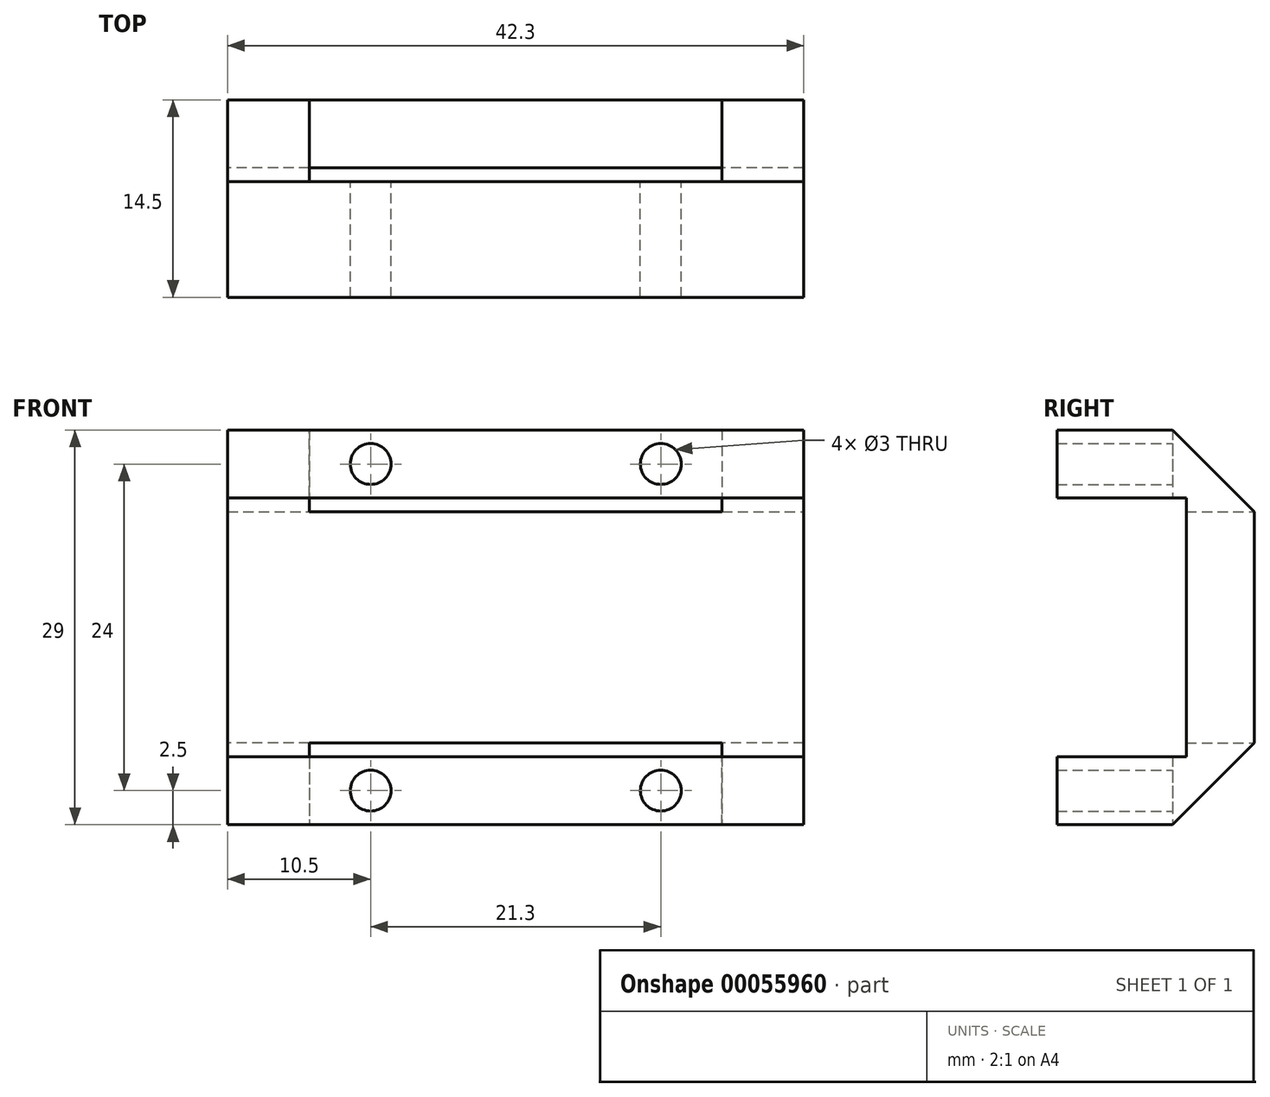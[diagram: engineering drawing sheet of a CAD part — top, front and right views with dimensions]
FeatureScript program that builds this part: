
annotation { "Feature Type Name" : "Feature", "Feature Type Description" : "" }
export const myFeature = defineFeature(function(context is Context, id is Id, definition is map)
    precondition{}
    {
        {
            var Q0;
            Q0=qCreatedBy(makeId("Right.planeOp"),FACE);
            var sketch = newSketch(context, id + "F0", { "sketchPlane" : qUnion([Q0])});
            skLineSegment(sketch, "E0.rect.bottom", {"start": v(9.5, 9.5) * mm, "end": v(0, 9.5) * mm});
            skLineSegment(sketch, "E0.rect.top", {"start": v(9.5, -9.5) * mm, "end": v(0, -9.5) * mm});
            skLineSegment(sketch, "E0.rect.left", {"start": v(9.5, 9.5) * mm, "end": v(9.5, -9.5) * mm});
            skPoint(sketch, "E0.rect.middle", {"position": v(0, 0) * mm});
            skLineSegment(sketch, "E1.rect.bottom", {"start": v(14.5, 14.5) * mm, "end": v(0, 14.5) * mm});
            skLineSegment(sketch, "E1.rect.top", {"start": v(14.5, -14.5) * mm, "end": v(0, -14.5) * mm});
            skLineSegment(sketch, "E1.rect.left", {"start": v(14.5, 14.5) * mm, "end": v(14.5, -14.5) * mm});
            skLineSegment(sketch, "E2", {"start": v(0, 9.5) * mm, "end": v(0, 14.5) * mm});
            skLineSegment(sketch, "E3", {"start": v(0, -9.5) * mm, "end": v(0, -14.5) * mm});
            skSolve(sketch);
        }
        {
            var Q0;
            Q0=makeQuery(id+"F0.imprint","IMPRINT",FACE,{"disambiguationData":[TD([[makeQuery(id+"F0.imprint","IMPRINT",EDGE,{"derivedFrom":sQuery(id+"F0.wireOp",EDGE,"5346ee42-6b44-4ab4-b06a-5ea702be0697.bottom")}),1.0]])]});
            var Q1;
            Q1=makeQuery(id+"F0.imprint","IMPRINT",FACE,{"disambiguationData":[TD([[makeQuery(id+"F0.imprint","IMPRINT",EDGE,{"derivedFrom":sQuery(id+"F0.wireOp",EDGE,"9599e187-f427-41b1-8912-62db417e26b9.bottom")}),1.0]])]});
            var Q2;
            Q2=makeQuery(id+"F0.imprint","IMPRINT",FACE,{"disambiguationData":[TD([[makeQuery(id+"F0.imprint","IMPRINT",EDGE,{"derivedFrom":sQuery(id+"F0.wireOp",EDGE,"E0.rect.bottom")}),-1.0]])]});
            extrude(context, id + "F1", {"entities" : qUnion([Q0, Q1, Q2]), "depth" : 42.3 * mm});
        }
        {
            var Q0;
            Q0=makeQuery(id+"F1.opExtrude","SWEPT_FACE",FACE,{"disambiguationData":[OSD([sQuery(id+"F0.wireOp",EDGE,"E1.rect.left")])]});
            var sketch = newSketch(context, id + "F2", { "sketchPlane" : qUnion([Q0])});
            skLineSegment(sketch, "E4.bottom", {"start": v(-42.3, 14.5) * mm, "end": v(-36.3, 14.5) * mm, "construction": true});
            skLineSegment(sketch, "E4.top", {"start": v(-42.3, 8.5) * mm, "end": v(-36.3, 8.5) * mm, "construction": true});
            skLineSegment(sketch, "E4.left", {"start": v(-42.3, 14.5) * mm, "end": v(-42.3, 8.5) * mm, "construction": true});
            skLineSegment(sketch, "E4.right", {"start": v(-36.3, 14.5) * mm, "end": v(-36.3, 8.5) * mm, "construction": true});
            skLineSegment(sketch, "E5.bottom", {"start": v(0, 14.5) * mm, "end": v(-6, 14.5) * mm, "construction": true});
            skLineSegment(sketch, "E5.top", {"start": v(0, 8.5) * mm, "end": v(-6, 8.5) * mm, "construction": true});
            skLineSegment(sketch, "E5.left", {"start": v(0, 14.5) * mm, "end": v(0, 8.5) * mm, "construction": true});
            skLineSegment(sketch, "E5.right", {"start": v(-6, 14.5) * mm, "end": v(-6, 8.5) * mm, "construction": true});
            skLineSegment(sketch, "E6.bottom", {"start": v(0, -14.5) * mm, "end": v(-6, -14.5) * mm, "construction": true});
            skLineSegment(sketch, "E6.top", {"start": v(0, -8.5) * mm, "end": v(-6, -8.5) * mm, "construction": true});
            skLineSegment(sketch, "E6.left", {"start": v(0, -14.5) * mm, "end": v(0, -8.5) * mm, "construction": true});
            skLineSegment(sketch, "E6.right", {"start": v(-6, -14.5) * mm, "end": v(-6, -8.5) * mm, "construction": true});
            skLineSegment(sketch, "E7.bottom", {"start": v(-42.3, -14.5) * mm, "end": v(-36.3, -14.5) * mm, "construction": true});
            skLineSegment(sketch, "E7.top", {"start": v(-42.3, -8.5) * mm, "end": v(-36.3, -8.5) * mm, "construction": true});
            skLineSegment(sketch, "E7.left", {"start": v(-42.3, -14.5) * mm, "end": v(-42.3, -8.5) * mm, "construction": true});
            skLineSegment(sketch, "E7.right", {"start": v(-36.3, -14.5) * mm, "end": v(-36.3, -8.5) * mm, "construction": true});
            skLineSegment(sketch, "E8.bottom", {"start": v(-36.3, 14.5) * mm, "end": v(-6, 14.5) * mm});
            skLineSegment(sketch, "E8.top", {"start": v(-36.3, 8.5) * mm, "end": v(-6, 8.5) * mm});
            skLineSegment(sketch, "E8.left", {"start": v(-36.3, 14.5) * mm, "end": v(-36.3, 8.5) * mm});
            skLineSegment(sketch, "E8.right", {"start": v(-6, 14.5) * mm, "end": v(-6, 8.5) * mm});
            skLineSegment(sketch, "E9.bottom", {"start": v(-36.3, -8.5) * mm, "end": v(-6, -8.5) * mm});
            skLineSegment(sketch, "E9.top", {"start": v(-36.3, -14.5) * mm, "end": v(-6, -14.5) * mm});
            skLineSegment(sketch, "E9.left", {"start": v(-36.3, -8.5) * mm, "end": v(-36.3, -14.5) * mm});
            skLineSegment(sketch, "E9.right", {"start": v(-6, -8.5) * mm, "end": v(-6, -14.5) * mm});
            skSolve(sketch);
        }
        {
            var Q0;
            Q0=makeQuery(id+"F2.imprint","IMPRINT",FACE,{"disambiguationData":[TD([[makeQuery(id+"F2.imprint","IMPRINT",EDGE,{"derivedFrom":sQuery(id+"F2.wireOp",EDGE,"E8.bottom")}),-1.0]])]});
            var Q1;
            Q1=makeQuery(id+"F2.imprint","IMPRINT",FACE,{"disambiguationData":[TD([[makeQuery(id+"F2.imprint","IMPRINT",EDGE,{"derivedFrom":sQuery(id+"F2.wireOp",EDGE,"E9.bottom")}),-1.0]])]});
            extrude(context, id + "F3", {"entities" : qUnion([Q0, Q1]), "operationType" : NewBodyOperationType.REMOVE, "oppositeDirection" : true, "depth" : 6 * mm});
        }
        {
            var Q0;
            {var subQ0=sQuery(id+"F0.wireOp",EDGE,"E1.rect.left");var subQ1=sQuery(id+"F0.wireOp",EDGE,"E1.rect.top");Q0=makeQuery(id+"F3.boolean.opBoolean","SPLIT",EDGE,{"disambiguationData":[TD([makeQuery(id+"F3.opExtrude","SWEPT_FACE",FACE,{"disambiguationData":[OSD([sQuery(id+"F2.wireOp",EDGE,"E9.right")])]})])],"derivedFrom":makeQuery(id+"F1.opExtrude","SWEPT_EDGE",EDGE,{"disambiguationData":[OSD([subQ1,subQ0])]})});}
            var Q1;
            {var subQ0=sQuery(id+"F0.wireOp",EDGE,"E1.rect.left");var subQ1=sQuery(id+"F0.wireOp",EDGE,"E1.rect.top");Q1=makeQuery(id+"F3.boolean.opBoolean","SPLIT",EDGE,{"disambiguationData":[TD([makeQuery(id+"F3.opExtrude","SWEPT_FACE",FACE,{"disambiguationData":[OSD([sQuery(id+"F2.wireOp",EDGE,"E9.left")])]})])],"derivedFrom":makeQuery(id+"F1.opExtrude","SWEPT_EDGE",EDGE,{"disambiguationData":[OSD([subQ1,subQ0])]})});}
            var Q2;
            {var subQ0=sQuery(id+"F0.wireOp",EDGE,"E1.rect.left");var subQ1=sQuery(id+"F0.wireOp",EDGE,"E1.rect.bottom");Q2=makeQuery(id+"F3.boolean.opBoolean","SPLIT",EDGE,{"disambiguationData":[TD([makeQuery(id+"F3.opExtrude","SWEPT_FACE",FACE,{"disambiguationData":[OSD([sQuery(id+"F2.wireOp",EDGE,"E8.left")])]})])],"derivedFrom":makeQuery(id+"F1.opExtrude","SWEPT_EDGE",EDGE,{"disambiguationData":[OSD([subQ1,subQ0])]})});}
            var Q3;
            {var subQ0=sQuery(id+"F0.wireOp",EDGE,"E1.rect.left");var subQ1=sQuery(id+"F0.wireOp",EDGE,"E1.rect.bottom");Q3=makeQuery(id+"F3.boolean.opBoolean","SPLIT",EDGE,{"disambiguationData":[TD([makeQuery(id+"F3.opExtrude","SWEPT_FACE",FACE,{"disambiguationData":[OSD([sQuery(id+"F2.wireOp",EDGE,"E8.right")])]})])],"derivedFrom":makeQuery(id+"F1.opExtrude","SWEPT_EDGE",EDGE,{"disambiguationData":[OSD([subQ1,subQ0])]})});}
            chamfer(context, id + "F4", {"entities" : qUnion([Q0, Q1, Q2, Q3]), "width" : 6 * mm, "tangentPropagation" : true});
        }
        {
            var Q0;
            Q0=makeQuery(id+"F3.boolean.opBoolean","COPY",FACE,{"derivedFrom":makeQuery(id+"F3.opExtrude","CAP_FACE",FACE,{"disambiguationData":[OSD([sQuery(id+"F2.wireOp",EDGE,"E8.bottom"),sQuery(id+"F2.wireOp",EDGE,"E8.top"),sQuery(id+"F2.wireOp",EDGE,"E8.left"),sQuery(id+"F2.wireOp",EDGE,"E8.right")])],"isStart":false})});
            var sketch = newSketch(context, id + "F5", { "sketchPlane" : qUnion([Q0])});
            skLineSegment(sketch, "E10", {"start": v(-36.3, 14.5) * mm, "end": v(-34.3, 14.5) * mm, "construction": true});
            skLineSegment(sketch, "E11", {"start": v(-34.3, 14.5) * mm, "end": v(-29.3, 14.5) * mm, "construction": true});
            skLineSegment(sketch, "E12", {"start": v(-29.3, 14.5) * mm, "end": v(-13, 14.5) * mm, "construction": true});
            skLineSegment(sketch, "E13", {"start": v(-13, 14.5) * mm, "end": v(-8, 14.5) * mm, "construction": true});
            skLineSegment(sketch, "E14", {"start": v(-8, 14.5) * mm, "end": v(-6, 14.5) * mm, "construction": true});
            skLineSegment(sketch, "E15", {"start": v(-34.3, 14.5) * mm, "end": v(-29.3, 9.5) * mm, "construction": true});
            skLineSegment(sketch, "E16", {"start": v(-13, 14.5) * mm, "end": v(-8, 9.5) * mm, "construction": true});
            skCircle(sketch, "E17", {"center": v(-31.8, 12) * mm, "radius": 1.5 * mm});
            skCircle(sketch, "E18", {"center": v(-10.5, 12) * mm, "radius": 1.5 * mm});
            skSolve(sketch);
        }
        {
            var Q0;
            Q0=makeQuery(id+"F5.imprint","IMPRINT",FACE,{"disambiguationData":[TD([[makeQuery(id+"F5.imprint","IMPRINT",EDGE,{"derivedFrom":sQuery(id+"F5.wireOp",EDGE,"E17")}),1.0]])]});
            var Q1;
            Q1=makeQuery(id+"F5.imprint","IMPRINT",FACE,{"disambiguationData":[TD([[makeQuery(id+"F5.imprint","IMPRINT",EDGE,{"derivedFrom":sQuery(id+"F5.wireOp",EDGE,"E18")}),1.0]])]});
            extrude(context, id + "F6", {"entities" : qUnion([Q0, Q1]), "operationType" : NewBodyOperationType.REMOVE, "endBound" : BoundingType.THROUGH_ALL, "oppositeDirection" : true, "depth" : 25 * mm});
        }
        {
            var Q0;
            Q0=makeQuery(id+"F3.boolean.opBoolean","COPY",FACE,{"derivedFrom":makeQuery(id+"F3.opExtrude","CAP_FACE",FACE,{"disambiguationData":[OSD([sQuery(id+"F2.wireOp",EDGE,"E9.bottom"),sQuery(id+"F2.wireOp",EDGE,"E9.top"),sQuery(id+"F2.wireOp",EDGE,"E9.left"),sQuery(id+"F2.wireOp",EDGE,"E9.right")])],"isStart":false})});
            var sketch = newSketch(context, id + "F7", { "sketchPlane" : qUnion([Q0])});
            skLineSegment(sketch, "E19", {"start": v(-36.3, -14.5) * mm, "end": v(-34.3, -14.5) * mm, "construction": true});
            skLineSegment(sketch, "E20", {"start": v(-34.3, -14.5) * mm, "end": v(-29.3, -14.5) * mm, "construction": true});
            skLineSegment(sketch, "E21", {"start": v(-29.3, -14.5) * mm, "end": v(-13, -14.5) * mm, "construction": true});
            skLineSegment(sketch, "E22", {"start": v(-13, -14.5) * mm, "end": v(-8, -14.5) * mm, "construction": true});
            skLineSegment(sketch, "E23", {"start": v(-8, -14.5) * mm, "end": v(-6, -14.5) * mm, "construction": true});
            skLineSegment(sketch, "E24", {"start": v(-34.3, -14.5) * mm, "end": v(-29.3, -9.5) * mm, "construction": true});
            skLineSegment(sketch, "E25", {"start": v(-13, -14.5) * mm, "end": v(-8, -9.5) * mm, "construction": true});
            skCircle(sketch, "E26", {"center": v(-31.8, -12) * mm, "radius": 1.5 * mm});
            skCircle(sketch, "E27", {"center": v(-10.5, -12) * mm, "radius": 1.5 * mm});
            skSolve(sketch);
        }
        {
            var Q0;
            Q0=makeQuery(id+"F7.imprint","IMPRINT",FACE,{"disambiguationData":[TD([[makeQuery(id+"F7.imprint","IMPRINT",EDGE,{"derivedFrom":sQuery(id+"F7.wireOp",EDGE,"E26")}),1.0]])]});
            var Q1;
            Q1=makeQuery(id+"F7.imprint","IMPRINT",FACE,{"disambiguationData":[TD([[makeQuery(id+"F7.imprint","IMPRINT",EDGE,{"derivedFrom":sQuery(id+"F7.wireOp",EDGE,"E27")}),1.0]])]});
            extrude(context, id + "F8", {"entities" : qUnion([Q0, Q1]), "operationType" : NewBodyOperationType.REMOVE, "endBound" : BoundingType.THROUGH_ALL, "oppositeDirection" : true, "depth" : 25 * mm});
        }
    });
